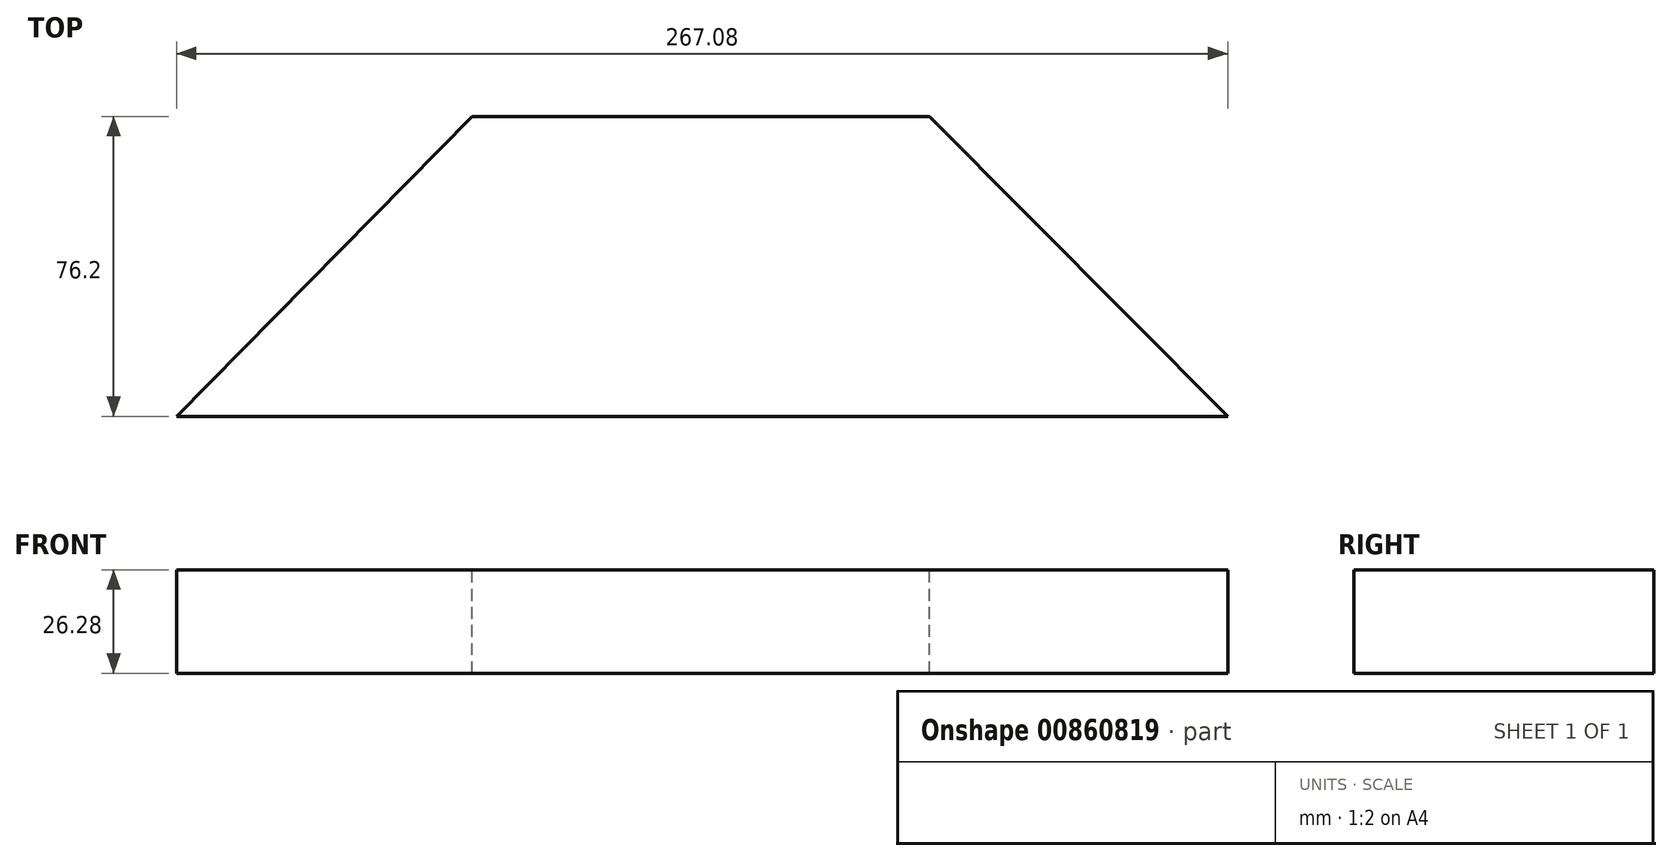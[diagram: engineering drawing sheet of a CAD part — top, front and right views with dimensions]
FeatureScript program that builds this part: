
annotation { "Feature Type Name" : "Feature", "Feature Type Description" : "" }
export const myFeature = defineFeature(function(context is Context, id is Id, definition is map)
    precondition{}
    {
        {
            var Q0;
            Q0=qCreatedBy(makeId("Front.planeOp"),FACE);
            var sketch = newSketch(context, id + "F0", { "sketchPlane" : qUnion([Q0])});
            skLineSegment(sketch, "E0", {"start": v(0, 0) * mm, "end": v(-267.08, 0) * mm});
            skLineSegment(sketch, "E1", {"start": v(-267.08, 0) * mm, "end": v(-267.08, 26.28) * mm});
            skLineSegment(sketch, "E2", {"start": v(-267.08, 26.28) * mm, "end": v(0, 26.28) * mm});
            skLineSegment(sketch, "E3", {"start": v(0, 26.28) * mm, "end": v(0, 0) * mm});
            skSolve(sketch);
        }
        {
            var Q0;
            Q0 = qSketchRegion(id + "F0", true);
            extrude(context, id + "F1", {"entities" : qUnion([Q0]), "depth" : 76.2 * mm, "offsetDistance" : 25.4 * mm});
        }
        {
            var Q0;
            Q0=makeQuery(id+"F1.opExtrude","SWEPT_FACE",FACE,{"disambiguationData":[OSD([sQuery(id+"F0.wireOp",EDGE,"E2")])]});
            var sketch = newSketch(context, id + "F2", { "sketchPlane" : qUnion([Q0])});
            skLineSegment(sketch, "E4", {"start": v(-267.08, 0) * mm, "end": v(-192.03, 0) * mm});
            skLineSegment(sketch, "E5", {"start": v(0, 0) * mm, "end": v(-75.82, 0) * mm});
            skLineSegment(sketch, "E6", {"start": v(-75.82, 0) * mm, "end": v(0, -76.2) * mm});
            skLineSegment(sketch, "E7", {"start": v(-192.03, 0) * mm, "end": v(-267.08, -76.2) * mm});
            skLineSegment(sketch, "E8", {"start": v(-267.08, -76.2) * mm, "end": v(-267.08, 0) * mm});
            skLineSegment(sketch, "E9", {"start": v(0, 0) * mm, "end": v(0, -76.2) * mm});
            skSolve(sketch);
        }
        {
            var Q0;
            Q0 = qSketchRegion(id + "F2", true);
            extrude(context, id + "F3", {"entities" : qUnion([Q0]), "operationType" : NewBodyOperationType.REMOVE, "oppositeDirection" : true, "depth" : 50.8 * mm, "offsetDistance" : 25.4 * mm});
        }
    });
